SOLIDWORKS PART (.sldprt)
format: sldprt  version: not decoded by parser v0  size: 124,928 bytes
history: native  units: mm
features: plane x5, sketch x4, material x1, extrude x1, cut_extrude x1, sweep x1, mirror x1, pattern_linear x1 (+8 scaffold rows collapsed)
feature tree (23):
  scaffold x8  (default folders/planes/origin — collapsed)
  material  "Matériau <non spécifié>"
  plane  "Plan de face"
  plane  "Plan de dessus"
  plane  "Plan de droite"
  sketch  "Esquisse1"  dims[D1=3.0mm D2=6.0mm D3=3.2mm]
  extrude  "Extrusion1"  Depth=10mm
  sketch  "Esquisse2"  dims[D1=~0.36258mm]
  cut_extrude  "Enlèv. mat.-Extru.1"  Depth=0.5mm
  sketch  "Esquisse3"  dims[D3=~0.315726mm D1=1.6mm D2=1.16mm]
  plane  "Plan1"  Offset=1.16mm
  sketch  "Esquisse5"  dims[D1=4.0mm D2=0.65mm]
  sweep  "Balayage1"
  plane  "Plan2"
  mirror  "Symétrie1"
  pattern_linear  "Répétition linéaire1"  Count1=4 Count2=1 Spacing1=2.54mm Spacing2=50mm
decode coverage: 7 of 9 modeling features carry decoded parameters
note: ~ marks probable driven/reference dimensions
note: suppression state not decoded; provenance and decode notes live in map.json
